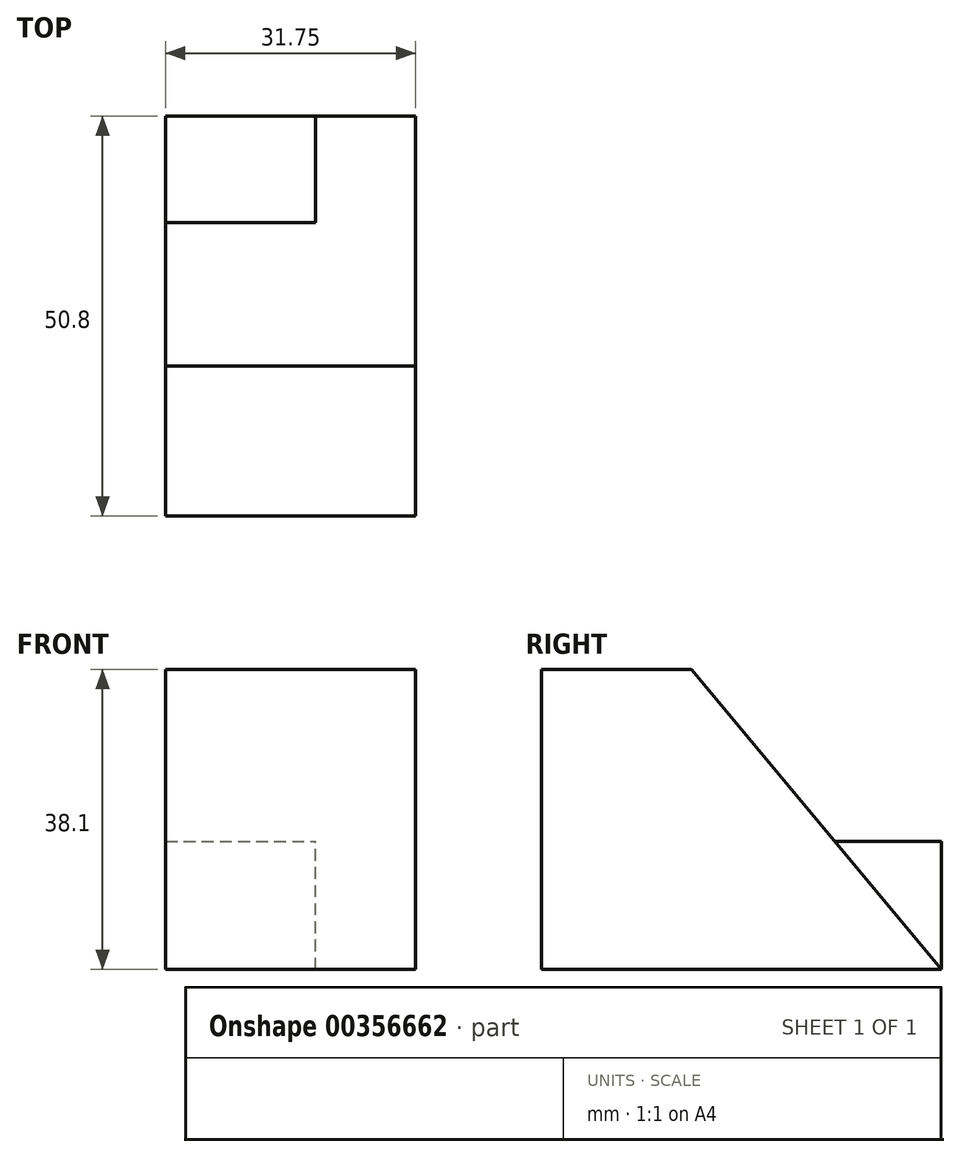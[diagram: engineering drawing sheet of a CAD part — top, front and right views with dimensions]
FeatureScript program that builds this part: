
annotation { "Feature Type Name" : "Feature", "Feature Type Description" : "" }
export const myFeature = defineFeature(function(context is Context, id is Id, definition is map)
    precondition{}
    {
        {
            var Q0;
            Q0=qCreatedBy(makeId("Right.planeOp"),FACE);
            var sketch = newSketch(context, id + "F0", { "sketchPlane" : qUnion([Q0])});
            skLineSegment(sketch, "E0", {"start": v(33.5, 21.84) * mm, "end": v(-17.3, 21.84) * mm});
            skLineSegment(sketch, "E1", {"start": v(-17.3, 21.84) * mm, "end": v(-17.3, -16.26) * mm});
            skLineSegment(sketch, "E2", {"start": v(-17.3, -16.26) * mm, "end": v(33.5, -16.26) * mm});
            skLineSegment(sketch, "E3", {"start": v(33.5, -16.26) * mm, "end": v(33.5, 21.84) * mm});
            skSolve(sketch);
        }
        {
            var Q0;
            Q0=makeQuery(id+"F0.imprint","IMPRINT",FACE,{"disambiguationData":[TD([[makeQuery(id+"F0.imprint","IMPRINT",EDGE,{"derivedFrom":sQuery(id+"F0.wireOp",EDGE,"E0")}),1.0]])]});
            extrude(context, id + "F1", {"entities" : qUnion([Q0]), "depth" : 31.75 * mm});
        }
        {
            var Q0;
            Q0=makeQuery(id+"F1.opExtrude","CAP_FACE",FACE,{"disambiguationData":[OSD([sQuery(id+"F0.wireOp",EDGE,"E0"),sQuery(id+"F0.wireOp",EDGE,"E1"),sQuery(id+"F0.wireOp",EDGE,"E2"),sQuery(id+"F0.wireOp",EDGE,"E3")])],"isStart":false});
            var sketch = newSketch(context, id + "F2", { "sketchPlane" : qUnion([Q0])});
            skLineSegment(sketch, "E4", {"start": v(-17.3, 21.84) * mm, "end": v(1.74, 21.84) * mm});
            skLineSegment(sketch, "E5", {"start": v(1.74, 21.84) * mm, "end": v(33.5, -16.26) * mm});
            skSolve(sketch);
        }
        {
            var Q0;
            {var subQ0=sQuery(id+"F2.wireOp",EDGE,"E5");Q0=makeQuery(id+"F2.imprint","IMPRINT",FACE,{"disambiguationData":[TD([[makeQuery(id+"F2.imprint","IMPRINT",EDGE,{"derivedFrom":subQ0}),1.0]])]});}
            extrude(context, id + "F3", {"entities" : qUnion([Q0]), "operationType" : NewBodyOperationType.REMOVE, "oppositeDirection" : true, "depth" : 12.7 * mm});
        }
        {
            var Q0;
            Q0=makeQuery(id+"F3.boolean.opBoolean","COPY",FACE,{"derivedFrom":makeQuery(id+"F3.opExtrude","CAP_FACE",FACE,{"disambiguationData":[OSD([sQuery(id+"F0.wireOp",EDGE,"E0"),sQuery(id+"F0.wireOp",EDGE,"E3"),sQuery(id+"F2.wireOp",EDGE,"E5")])],"isStart":false})});
            var sketch = newSketch(context, id + "F4", { "sketchPlane" : qUnion([Q0])});
            skLineSegment(sketch, "E6", {"start": v(33.5, 0) * mm, "end": v(19.94, 0) * mm});
            skPoint(sketch, "E6.startSnap0", {"position": v(33.5, 2.79) * mm});
            skLineSegment(sketch, "E7", {"start": v(19.94, 0) * mm, "end": v(1.74, 21.84) * mm});
            skLineSegment(sketch, "E8", {"start": v(1.74, 21.84) * mm, "end": v(33.5, 21.84) * mm});
            skLineSegment(sketch, "E9", {"start": v(33.5, 21.84) * mm, "end": v(33.5, 0) * mm});
            skSolve(sketch);
        }
        {
            var Q0;
            Q0=makeQuery(id+"F4.imprint","IMPRINT",FACE,{"disambiguationData":[TD([[makeQuery(id+"F4.imprint","IMPRINT",EDGE,{"derivedFrom":sQuery(id+"F4.wireOp",EDGE,"E6")}),-1.0]])]});
            extrude(context, id + "F5", {"entities" : qUnion([Q0]), "operationType" : NewBodyOperationType.REMOVE, "oppositeDirection" : true, "depth" : 25.4 * mm});
        }
    });
